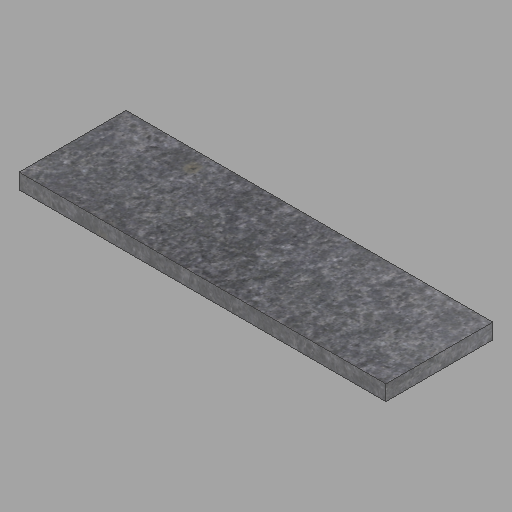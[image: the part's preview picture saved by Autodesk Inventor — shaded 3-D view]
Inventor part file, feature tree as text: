
AUTODESK INVENTOR PART (.ipt)
format: ipt  version: 2023 (Build 270158000, 158)  size: 202,752 bytes
history: native  units: in
note: dims shown in document units (in); Inventor stores cm internally (conversion verified against a paired STEP export)
features: other x1, extrude x1, sketch x1
ambient origin geometry x8: Origin, YZ Plane, XZ Plane, XY Plane, X Axis, Y Axis, Z Axis, Center Point
bodies: Solid1 (feature_tree)
feature tree (3):
  other  "2x14x48-3"
  extrude  "Extrusion1"  Depth=14.0in
  sketch  "Sketch1"  dims[d0=2.0in d1=14.0in d2=48.0in d3=0.0in]
